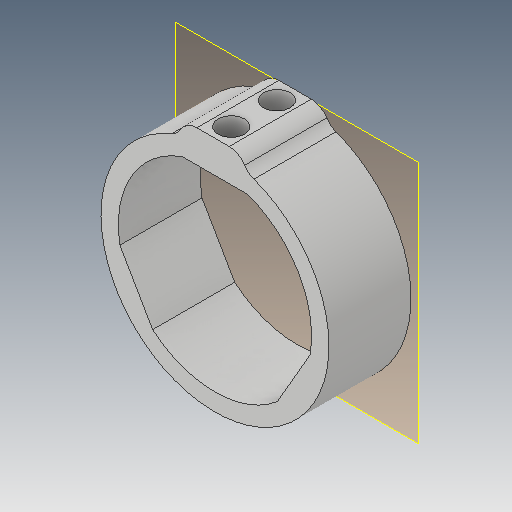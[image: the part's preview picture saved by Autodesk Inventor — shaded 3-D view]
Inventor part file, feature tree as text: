
AUTODESK INVENTOR PART (.ipt)
format: ipt  version: 2019.4 (Build 234330000, 330)  size: 162,816 bytes
history: native  units: mm
features: other x4, extrude x3, reference x3, sketch x2, plane x1, pattern_circular x1, fillet x1, projected_geometry x1
ambient origin geometry x8: Origin, YZ Plane, XZ Plane, XY Plane, X Axis, Y Axis, Z Axis, Center Point
bodies: Solid1 (feature_tree)
feature tree (16):
  plane  "Work Plane2"
  extrude  "Extrusion1"  Depth=9.0mm TaperAngle=0.0deg
  pattern_circular  "Circular Pattern1"  Count=3 Angle=360.0deg
  extrude  "Extrusion2"  Depth=10.0mm TaperAngle=0.0deg
  fillet  "Fillet1"  Radius=2.0mm
  extrude  "Extrusion3"  Depth=10.0mm TaperAngle=0.0deg
  reference  "Reference1"
  reference  "Reference2"
  reference  "Reference3"
  sketch  "Sketch3"  dims[d1=25.0mm d3=9.0mm d4=0.0mm d5=30.0mm d6=360.0deg]
  sketch  "Sketch4"  dims[d9=7.0mm d10=10.0mm d11=0.0mm d12=2.0mm d15=10.0mm d16=0.0mm d17=0.5mm d18=2.9mm d19=2.9mm d20=2.0mm d21=5.0mm]
  projected_geometry  "Projected Loop2"
  other  "Assembly_Opentrons_Autofocus_v1.iam"
  other  "Assembly_Autofocus_10x_laser_espcam_v1:1"
  other  "20_focus_inlet_linearflexure_objective_mount_v0:1"
  other  "00_objectivelens_10x:1"
